# Revit family: INOX LED
name_source: partatom
category: Осветительные приборы
revit_build: Autodesk Revit 2016 (Build: 20161004_0715(x64)
units: mm (PartAtom-declared; Revit-internal decimal feet)

## family parameters
Источник света = Нет
Общий = Нет
Основа = Грань
При загрузке вырезать с полостями = Нет
Размер круглого соединителя = Использовать диаметр
Тип детали = Нормальный
Точка расчета площади = Нет

## types (1)
- INOX LED
    ADSK_Единица измерения = Шт.
    ADSK_Завод-изготовитель = ООО МГК Световые технологии
    ADSK_Классификация нагрузок = Прочее
    ADSK_Код изделия = 1079000170
    ADSK_Количество фаз = 1
    ADSK_Количество фаз числовое = 1
    ADSK_Коэффициент мощности = 0.9
    ADSK_Масса = 4.4
    ADSK_Наименование = Серия светильников для тяжелых условий эксплуатации. Предназначены для применения на предприятиях химической, оборонной и пищевой промышленности. Возможно применение в пожароопасных зонах. Светильники INOX LED отличаются удобным монтажом благодаря креплению пластины с кластерами и источником питания к корпусу с помощью магнитов. Возможно изготовление различных модификаций с блоком защиты от перенапряжения (OVP), аварийным блоком (EM)
    ADSK_Напряжение = 230 В
    ADSK_Номинальная мощность = 0 кВт
    ADSK_Полная мощность = 0 кВ·А
    ADSK_Размер_Высота = 90 мм
    ADSK_Размер_Длина = 700 мм
    ADSK_Размер_Ширина = 210 мм
    ADSK_Ток = 0 А
    ADSK_Энергоэффективность = 76 лм/Вт
    IP Class = IP65
    URL = https://www.ltcompany.com
    Блок аварийного питания = Нет
    Выбор ИС = IES_INOX LED : 700 4000K 2600
    Группа модели = Светильники
    Да = Нет
    Изготовитель = ООО МГК Световые технологии
    Класс Защиты = I
    Класс пожароопасности = П-I,II,IIa,ІІІ
    Климатическая зона = УХЛ2
    Код по классификатору = D5020200
    Корпус = Cерый металл
    Нет = Нет
    Область использования = Паркинги / гаражи, Промышленные предприятия, Теплицы (растениеводство), Транспортные узлы (вокзалы, аэропорты)
    Описание = Серия светильников для тяжелых условий эксплуатации. Предназначены для применения на предприятиях химической, оборонной и пищевой промышленности. Возможно применение в пожароопасных зонах. Светильники INOX LED отличаются удобным монтажом благодаря креплению пластины с кластерами и источником питания к корпусу с помощью магнитов. Возможно изготовление различных модификаций с блоком защиты от перенапряжения (OVP), аварийным блоком (EM)
    Отметка по умолчанию = 0 мм
    Плафон = Плафон самосвечение
    Поворот.высота = 90 мм
    Подвес.материал = Cерый металл
    Подвес.ширина = 560 мм
    Полная установленная мощность = 0 кВ·А
    Скобы.высота = 10 мм
    Тип ИС = LED
    Тип ПРА = Драйвер
    Тип продукции = Светильник

## geometry (parser evidence)
native form markers: Blend x2
no freeform markers — native parametric forms only
